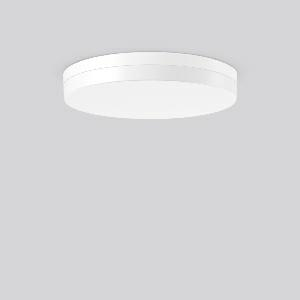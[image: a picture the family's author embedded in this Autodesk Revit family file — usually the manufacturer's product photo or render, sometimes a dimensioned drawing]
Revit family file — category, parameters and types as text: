
# Revit family: flat_slim_round_312634_002_19_e07c
name_source: partatom
category: Lighting Fixtures
units: mm (PartAtom-declared; Revit-internal decimal feet)

## family parameters
Cut with Voids When Loaded = No
Host = Face
Light Source = No
Part Type = Normal
Room Calculation Point = No
Round Connector Dimension = Use Diameter
Shared = No

## types (1)
- MultiLumen 1 830 (1 x LED Modul 830, 3450 lm, 3000)
    Apparent Load = 26 VA
    CIE Flux Codes = 40 71 90 84 100
    Color Rendering = 80
    Color Temperature = 3000
    Default Elevation = 1800 mm
    Height = 70 mm
    Lamp = 1 x LED Modul 830
    Lamp Light Flux = 3450 lm
    Lamp count = 1
    Length = 480 mm
    Lifetime = 50000 h
    Luminous efficacy = 133 lm/W
    Manufacturer = RZB
    ModVariant = No
    Model = 312634.002.19
    Mounting Place = Ceiling
    Mounting Type = Surface mounted
    Number of Poles = 1
    OnlyDefault = Yes
    Power Factor = 1
    Product Name = FLAT SLIM round
    Product group = Surface mounted ceiling and wall luminaires
    ProductGroupID = 305
    Protection Class = Protection class I
    Protection Degree = Degree of protection
    RLX_Detail_Level = 1
    RLX_Emergency_Light_Flux = 0 lm
    RLX_Emergency_Type = 0
    RLX_Emergency_Type_DB = No
    RlxData = <blob elided: 21877 chars, md5=363f37f3>
    Socket = socket
    Standby Power = 0 W
    System Light Flux = 3450 lm
    System Power = 26 W
    Type Comments = MultiLumen 1 830
    Type Image = 312633.002.jpg
    URL = http://relux.com
    VarID = multilumen_1_830
    Voltage = 0 V
    Weight = 0.00 kg
    Width = 0 mm  [stored 0 ft]

note: [stored X ft] marks values corroborated as IEEE doubles in the binary element streams (Revit-internal decimal feet)

## geometry (parser evidence)
native form markers: Blend x4, Sweep x13
no freeform markers — native parametric forms only
